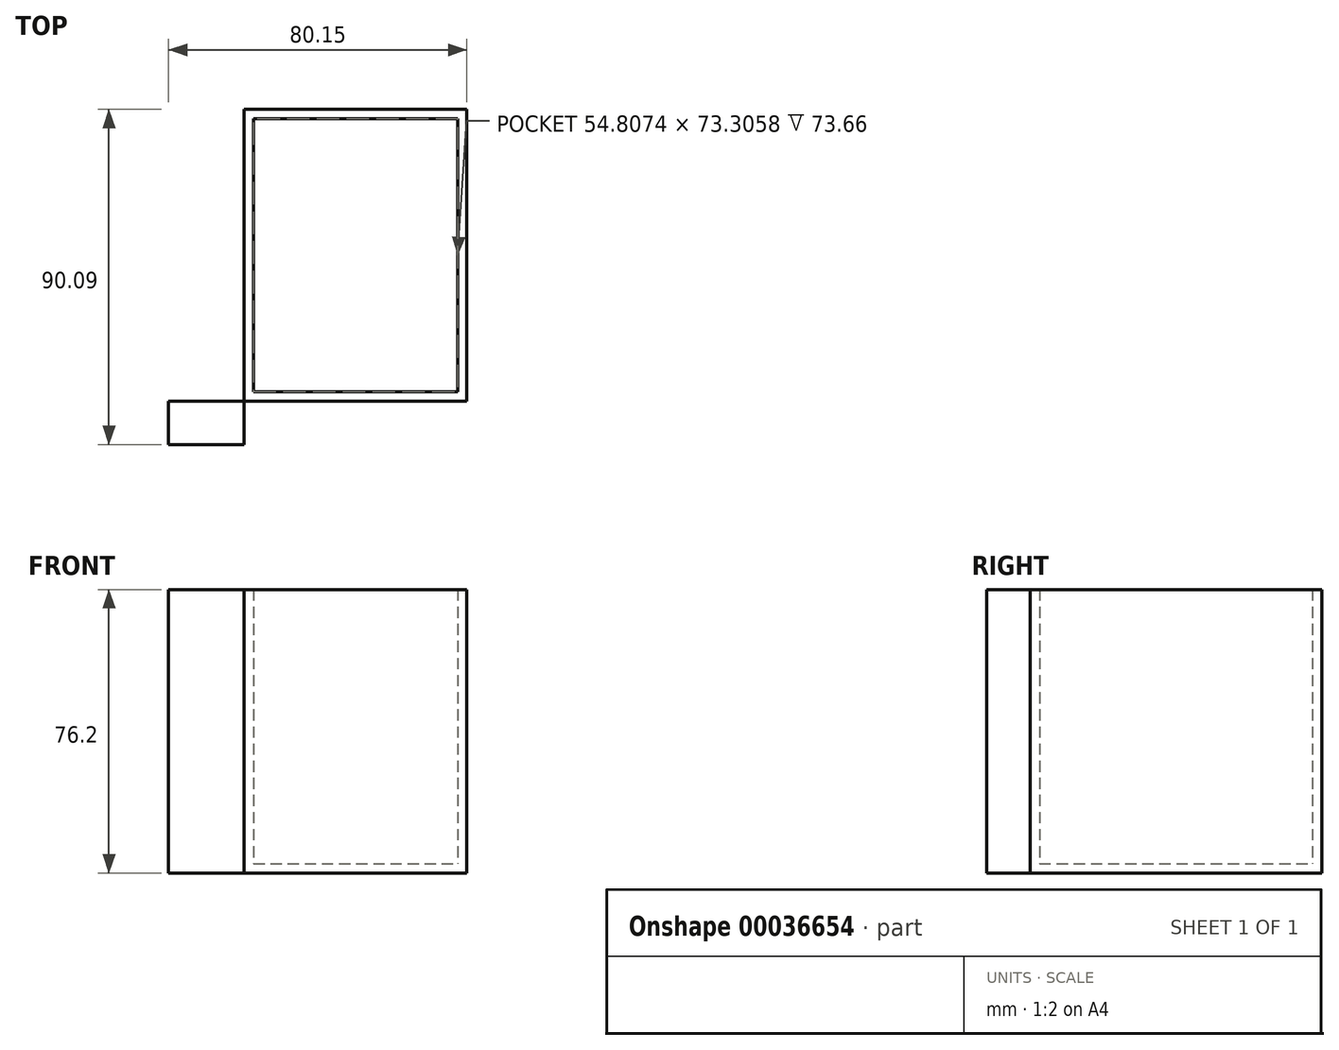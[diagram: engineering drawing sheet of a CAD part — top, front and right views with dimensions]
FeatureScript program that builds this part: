
annotation { "Feature Type Name" : "Feature", "Feature Type Description" : "" }
export const myFeature = defineFeature(function(context is Context, id is Id, definition is map)
    precondition{}
    {
        {
            var Q0;
            Q0=qCreatedBy(makeId("Top.planeOp"),FACE);
            var sketch = newSketch(context, id + "F0", { "sketchPlane" : qUnion([Q0])});
            skLineSegment(sketch, "E0.bottom", {"start": v(-35.55, -30.75) * mm, "end": v(-15.29, -30.75) * mm});
            skLineSegment(sketch, "E0.top", {"start": v(-35.55, -19.05) * mm, "end": v(-15.29, -19.05) * mm});
            skLineSegment(sketch, "E0.left", {"start": v(-35.55, -30.75) * mm, "end": v(-35.55, -19.05) * mm});
            skLineSegment(sketch, "E0.right", {"start": v(-15.29, -30.75) * mm, "end": v(-15.29, -19.05) * mm});
            skLineSegment(sketch, "E1.bottom", {"start": v(-15.29, -19.05) * mm, "end": v(44.6, -19.05) * mm});
            skLineSegment(sketch, "E1.top", {"start": v(-15.29, 59.34) * mm, "end": v(44.6, 59.34) * mm});
            skLineSegment(sketch, "E1.left", {"start": v(-15.29, -19.05) * mm, "end": v(-15.29, 59.34) * mm});
            skLineSegment(sketch, "E1.right", {"start": v(44.6, -19.05) * mm, "end": v(44.6, 59.34) * mm});
            skSolve(sketch);
        }
        {
            var Q0;
            Q0=makeQuery(id+"F0.imprint","IMPRINT",FACE,{"disambiguationData":[TD([[makeQuery(id+"F0.imprint","IMPRINT",EDGE,{"derivedFrom":sQuery(id+"F0.wireOp",EDGE,"E0.bottom")}),1.0]])]});
            var Q1;
            Q1=makeQuery(id+"F0.imprint","IMPRINT",FACE,{"disambiguationData":[TD([[makeQuery(id+"F0.imprint","IMPRINT",EDGE,{"derivedFrom":sQuery(id+"F0.wireOp",EDGE,"E1.bottom")}),1.0]])]});
            extrude(context, id + "F1", {"entities" : qUnion([Q0, Q1]), "depth" : 76.2 * mm});
        }
        {
            var Q0;
            Q0=makeQuery(id+"F1.opExtrude","CAP_FACE",FACE,{"disambiguationData":[OSD([sQuery(id+"F0.wireOp",EDGE,"E1.bottom"),sQuery(id+"F0.wireOp",EDGE,"E1.top"),sQuery(id+"F0.wireOp",EDGE,"E1.left"),sQuery(id+"F0.wireOp",EDGE,"E1.right")])],"isStart":false});
            shell(context, id + "F2", {"entities" : qUnion([Q0]), "thickness" : 2.54 * mm});
        }
    });
